# Revit family: ARKOSLIGHT_Magnetic 24V Micro Shaper 18-34
name_source: partatom
category: Lighting Fixtures
units: mm (PartAtom-declared; Revit-internal decimal feet)

## family parameters
Cut with Voids When Loaded = No
Host = Face
Light Source = No
Part Type = Normal
Room Calculation Point = No
Round Connector Dimension = Use Diameter
Shared = No

## types (1)
- ARKOSLIGHT_Magnetic 24V Micro Shaper 18-34
    ARKOSLIGHT_Apparent Load = 2 VA
    ARKOSLIGHT_Beam Angle = 34.00°
    ARKOSLIGHT_Body Color = ARKOSLIGHT_Black
    ARKOSLIGHT_CCT = 2700 K
    ARKOSLIGHT_CRI = CRI>90
    ARKOSLIGHT_Color = Black
    ARKOSLIGHT_Dimming = DIM options
    ARKOSLIGHT_Efficiency = 27%
    ARKOSLIGHT_Fixture Type = CEILING RECESSED
    ARKOSLIGHT_IES = A545-00-00 MAGNETIC 24V MICRO SHAPER 34 2700K CRI90.ies
    ARKOSLIGHT_IP = 20
    ARKOSLIGHT_Luminous flux = 190 lm
    ARKOSLIGHT_Model = MICRO SHAPER 24V
    ARKOSLIGHT_Reference = A5450000N
    ARKOSLIGHT_Series = MAGNETIC 24V SYSTEM
    ARKOSLIGHT_Wattage = 3 W
    Apparent Load = 2 VA
    Default Elevation = 0 mm  [stored 0 ft]
    IES = IES : A5450000N - MAGNETIC 24V MICRO SHAPER 18º-34º 2700K N
    Manufacturer = ARKOSLIGHT
    Model = MICRO SHAPER 24V
    URL = https://www.arkoslight.com

note: [stored X ft] marks values corroborated as IEEE doubles in the binary element streams (Revit-internal decimal feet)

## geometry (parser evidence)
native form markers: Sweep x16
no freeform markers — native parametric forms only
